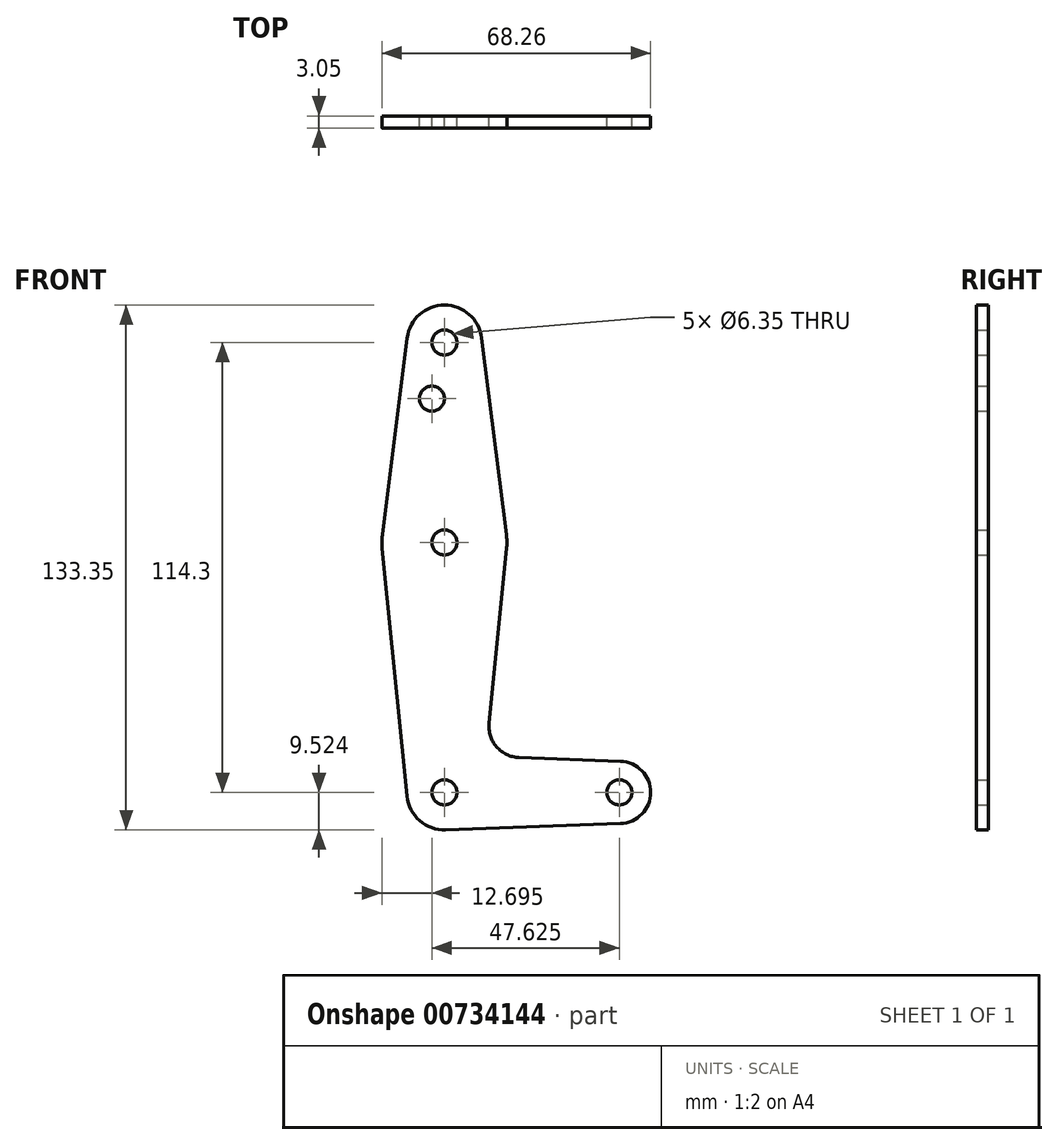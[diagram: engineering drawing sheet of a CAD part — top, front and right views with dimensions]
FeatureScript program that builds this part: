
annotation { "Feature Type Name" : "Feature", "Feature Type Description" : "" }
export const myFeature = defineFeature(function(context is Context, id is Id, definition is map)
    precondition{}
    {
        {
            var Q0;
            Q0=qCreatedBy(makeId("Front.planeOp"),FACE);
            var sketch = newSketch(context, id + "F0", { "sketchPlane" : qUnion([Q0])});
            skCircle(sketch, "E0", {"center": v(-28.12, -37.4) * mm, "radius": 9.53 * mm});
            skLineSegment(sketch, "E1", {"start": v(-28.12, -37.4) * mm, "end": v(16.33, -37.4) * mm, "construction": true});
            skLineSegment(sketch, "E2", {"start": v(-28.12, 76.9) * mm, "end": v(-28.12, -37.4) * mm, "construction": true});
            skCircle(sketch, "E3", {"center": v(-28.12, 76.9) * mm, "radius": 9.53 * mm});
            skCircle(sketch, "E4", {"center": v(-28.12, 26.1) * mm, "radius": 15.88 * mm});
            skCircle(sketch, "E5", {"center": v(16.33, -37.4) * mm, "radius": 7.94 * mm});
            skLineSegment(sketch, "E6", {"start": v(-18.67, 78.08) * mm, "end": v(-12.37, 28.08) * mm});
            skLineSegment(sketch, "E7", {"start": v(-37.57, 78.08) * mm, "end": v(-43.87, 28.08) * mm});
            skLineSegment(sketch, "E8", {"start": v(-43.92, 24.5) * mm, "end": v(-37.6, -38.36) * mm});
            skLineSegment(sketch, "E9", {"start": v(-12.32, 24.5) * mm, "end": v(-16.78, -19.81) * mm});
            skLineSegment(sketch, "E10", {"start": v(16.61, -29.47) * mm, "end": v(-9.15, -28.55) * mm});
            skLineSegment(sketch, "E11", {"start": v(16.61, -45.34) * mm, "end": v(-27.78, -46.93) * mm});
            skCircle(sketch, "E12", {"center": v(-31.3, 62.62) * mm, "radius": 3.18 * mm});
            skCircle(sketch, "E13", {"center": v(-28.12, 76.9) * mm, "radius": 3.18 * mm});
            skCircle(sketch, "E14", {"center": v(-28.12, 26.1) * mm, "radius": 3.18 * mm});
            skCircle(sketch, "E15", {"center": v(-28.12, -37.4) * mm, "radius": 3.18 * mm});
            skCircle(sketch, "E16", {"center": v(16.33, -37.4) * mm, "radius": 3.18 * mm});
            skArc(sketch, "E17.filletArc", {"start": v(-16.78, -19.81) * mm, "mid": v(-14.86, -25.83) * mm, "end": v(-9.15, -28.55) * mm});
            skSolve(sketch);
        }
        {
            var Q0;
            Q0 = qSketchRegion(id + "F0", true);
            extrude(context, id + "F1", {"entities" : qUnion([Q0]), "depth" : 3.05 * mm, "offsetDistance" : 25.4 * mm});
        }
    });
